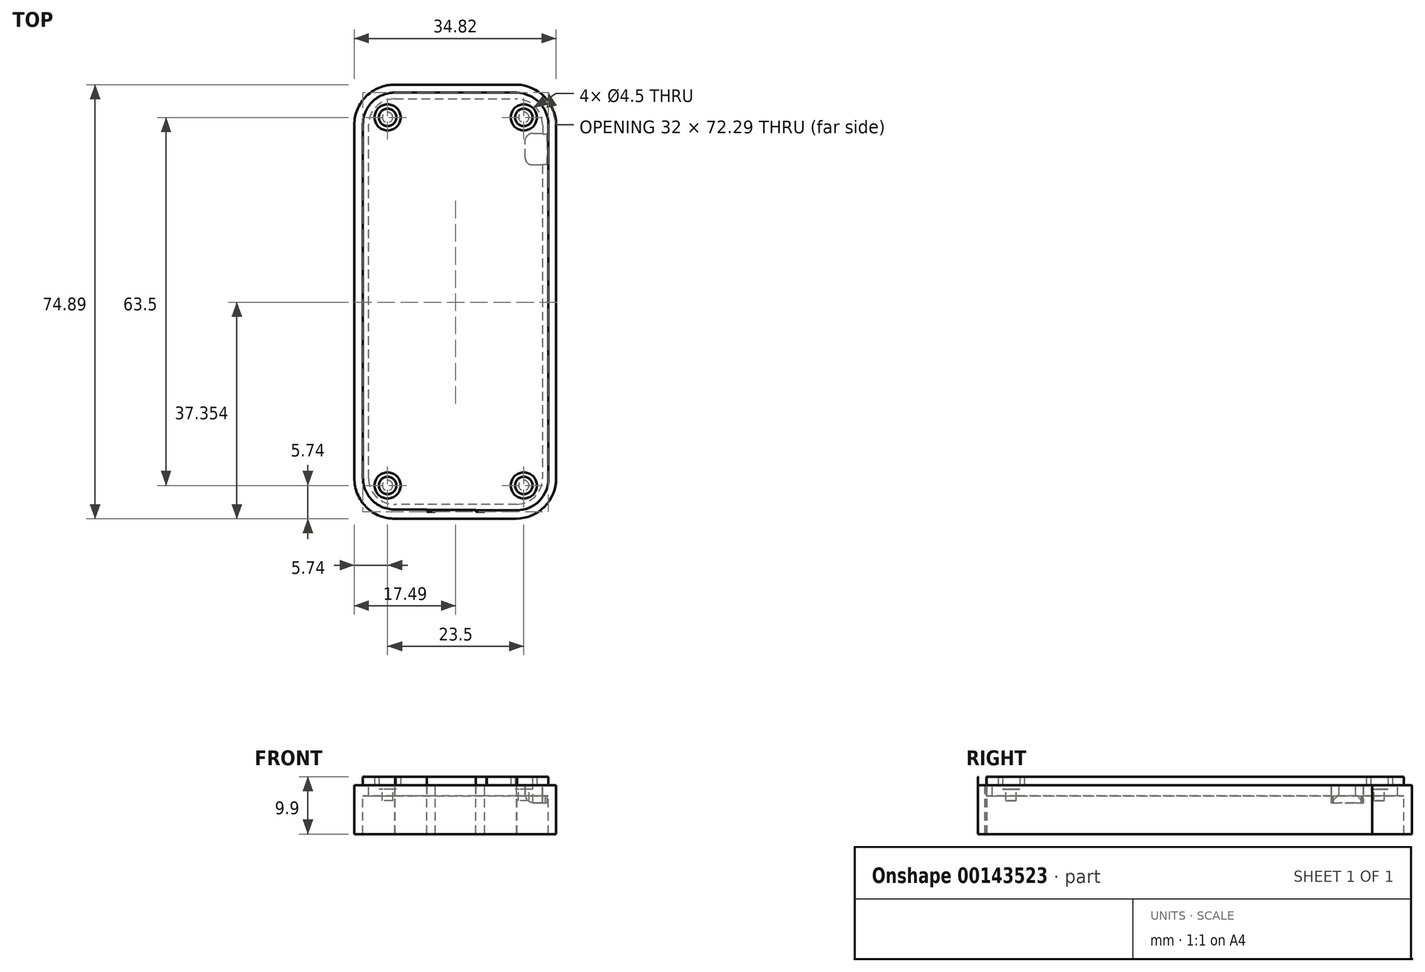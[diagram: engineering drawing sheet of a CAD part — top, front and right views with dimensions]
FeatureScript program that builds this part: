
annotation { "Feature Type Name" : "Feature", "Feature Type Description" : "" }
export const myFeature = defineFeature(function(context is Context, id is Id, definition is map)
    precondition{}
    {
        {
            var Q0;
            Q0=qCreatedBy(makeId("Top.planeOp"),FACE);
            var sketch = newSketch(context, id + "F0", { "sketchPlane" : qUnion([Q0])});
            skFitSpline(sketch, "E0", {"points": [v(15.77, 28.65) * mm, v(15.77, 28.68) * mm, v(15.76, 28.7) * mm, v(15.73, 28.76) * mm, v(15.71, 28.78) * mm, v(15.66, 28.82) * mm, v(15.62, 28.83) * mm, v(15.55, 28.85) * mm, v(15.5, 28.85) * mm, v(15.47, 28.85) * mm]});
            skFitSpline(sketch, "E1", {"points": [v(15.47, 23.65) * mm, v(15.5, 23.65) * mm, v(15.55, 23.65) * mm, v(15.62, 23.67) * mm, v(15.66, 23.68) * mm, v(15.71, 23.72) * mm, v(15.73, 23.74) * mm, v(15.76, 23.8) * mm, v(15.77, 23.82) * mm, v(15.77, 23.85) * mm]});
            skLineSegment(sketch, "E2", {"start": v(-3.5, -35.98) * mm, "end": v(3.5, -35.98) * mm});
            skLineSegment(sketch, "E3", {"start": v(-5.37, -37.49) * mm, "end": v(5.33, -37.49) * mm});
            skLineSegment(sketch, "E4", {"start": v(-5, -37.09) * mm, "end": v(-5, -36.28) * mm});
            skLineSegment(sketch, "E5", {"start": v(5, -36.02) * mm, "end": v(5, -37.12) * mm});
            skArc(sketch, "E6", {"start": v(5, -37.12) * mm, "mid": v(5.1, -37.4) * mm, "end": v(5.4, -37.49) * mm});
            skArc(sketch, "E7", {"start": v(-5.32, -37.49) * mm, "mid": v(-5.08, -37.35) * mm, "end": v(-5, -37.09) * mm});
            skLineSegment(sketch, "E8", {"start": v(14.96, 23.65) * mm, "end": v(15.42, 23.65) * mm});
            skLineSegment(sketch, "E9", {"start": v(15.01, 28.85) * mm, "end": v(15.47, 28.85) * mm});
            skLineSegment(sketch, "E10", {"start": v(14.96, 23.5) * mm, "end": v(14.96, 23.5) * mm});
            skLineSegment(sketch, "E11", {"start": v(14.96, 23.5) * mm, "end": v(13.33, 23.5) * mm});
            skEllipticalArc(sketch, "E12", {});
            skLineSegment(sketch, "E13", {"start": v(15, 29) * mm, "end": v(14.96, 29) * mm});
            skEllipticalArc(sketch, "E14", {});
            skLineSegment(sketch, "E15", {"start": v(13.33, 29) * mm, "end": v(14.96, 29) * mm});
            skFitSpline(sketch, "E16", {"points": [v(12, 27.7) * mm, v(12, 27.86) * mm, v(12.04, 28.05) * mm, v(12.16, 28.35) * mm, v(12.27, 28.5) * mm, v(12.5, 28.73) * mm, v(12.67, 28.84) * mm, v(12.97, 28.96) * mm, v(13.17, 29) * mm, v(13.33, 29) * mm]});
            skFitSpline(sketch, "E17", {"points": [v(13.33, 23.5) * mm, v(13.17, 23.5) * mm, v(12.97, 23.54) * mm, v(12.67, 23.66) * mm, v(12.5, 23.77) * mm, v(12.27, 24) * mm, v(12.16, 24.15) * mm, v(12.04, 24.45) * mm, v(12, 24.64) * mm, v(12, 24.8) * mm]});
            skEllipticalArc(sketch, "E18", {});
            skLineSegment(sketch, "E19", {"start": v(14.96, 23.65) * mm, "end": v(14.96, -30.5) * mm});
            skArc(sketch, "E20", {"start": v(10.53, -35.01) * mm, "mid": v(13.68, -33.67) * mm, "end": v(14.96, -30.5) * mm});
            skLineSegment(sketch, "E21", {"start": v(10.53, -35.01) * mm, "end": v(-10.47, -35.01) * mm});
            skArc(sketch, "E22", {"start": v(-15.01, -30.5) * mm, "mid": v(-13.69, -33.71) * mm, "end": v(-10.47, -35.01) * mm});
            skLineSegment(sketch, "E23", {"start": v(-15.01, -30.5) * mm, "end": v(-15.01, 30.5) * mm});
            skArc(sketch, "E24", {"start": v(-10.5, 34.93) * mm, "mid": v(-13.68, 33.65) * mm, "end": v(-15.01, 30.5) * mm});
            skLineSegment(sketch, "E25", {"start": v(-10.5, 34.93) * mm, "end": v(10.5, 34.93) * mm});
            skArc(sketch, "E26", {"start": v(15.01, 30.38) * mm, "mid": v(13.68, 33.58) * mm, "end": v(10.5, 34.93) * mm});
            skLineSegment(sketch, "E27", {"start": v(15.01, 30.38) * mm, "end": v(15.01, 28.87) * mm});
            skLineSegment(sketch, "E28", {"start": v(-5.37, -35.9) * mm, "end": v(-10.47, -35.9) * mm});
            skArc(sketch, "E29", {"start": v(-16, -30.4) * mm, "mid": v(-14.38, -34.31) * mm, "end": v(-10.47, -35.9) * mm});
            skLineSegment(sketch, "E30", {"start": v(-16, -30.4) * mm, "end": v(-16, 30.6) * mm});
            skArc(sketch, "E31", {"start": v(-10.5, 36) * mm, "mid": v(-14.37, 34.45) * mm, "end": v(-16, 30.6) * mm});
            skLineSegment(sketch, "E32", {"start": v(-10.5, 36) * mm, "end": v(10.5, 36) * mm});
            skArc(sketch, "E33", {"start": v(16, 30.48) * mm, "mid": v(14.38, 34.37) * mm, "end": v(10.5, 36) * mm});
            skLineSegment(sketch, "E34", {"start": v(16, 30.48) * mm, "end": v(16, -30.52) * mm});
            skArc(sketch, "E35", {"start": v(10.59, -36.02) * mm, "mid": v(14.43, -34.39) * mm, "end": v(16, -30.52) * mm});
            skLineSegment(sketch, "E36", {"start": v(5, -36.28) * mm, "end": v(3.5, -36.28) * mm});
            skLineSegment(sketch, "E37", {"start": v(3.5, -36.28) * mm, "end": v(3.5, -35.98) * mm});
            skLineSegment(sketch, "E38", {"start": v(-3.5, -35.98) * mm, "end": v(-3.5, -36.28) * mm});
            skLineSegment(sketch, "E39", {"start": v(-3.5, -36.28) * mm, "end": v(-5, -36.28) * mm});
            skLineSegment(sketch, "E40", {"start": v(15.78, 27.7) * mm, "end": v(15.78, 24.8) * mm});
            skLineSegment(sketch, "E41", {"start": v(12, 24.8) * mm, "end": v(12, 27.7) * mm});
            skCircle(sketch, "E42", {"center": v(-11.75, -31.75) * mm, "radius": 0.9 * mm});
            skCircle(sketch, "E43", {"center": v(11.75, -31.75) * mm, "radius": 0.9 * mm});
            skCircle(sketch, "E44", {"center": v(-11.75, 31.75) * mm, "radius": 0.9 * mm});
            skCircle(sketch, "E45", {"center": v(11.75, 31.75) * mm, "radius": 0.9 * mm});
            skCircle(sketch, "E46", {"center": v(11.75, -31.75) * mm, "radius": 1.5 * mm});
            skCircle(sketch, "E47", {"center": v(-11.75, -31.75) * mm, "radius": 1.5 * mm});
            skCircle(sketch, "E48", {"center": v(11.75, 31.75) * mm, "radius": 1.5 * mm});
            skCircle(sketch, "E49", {"center": v(-11.75, 31.75) * mm, "radius": 1.5 * mm});
            skCircle(sketch, "E50", {"center": v(11.75, -31.75) * mm, "radius": 2.25 * mm});
            skCircle(sketch, "E51", {"center": v(-11.75, -31.75) * mm, "radius": 2.25 * mm});
            skCircle(sketch, "E52", {"center": v(11.75, 31.75) * mm, "radius": 2.25 * mm});
            skCircle(sketch, "E53", {"center": v(-11.75, 31.75) * mm, "radius": 2.25 * mm});
            skLineSegment(sketch, "E54", {"start": v(10.43, -37.49) * mm, "end": v(5.33, -37.49) * mm});
            skLineSegment(sketch, "E55", {"start": v(-5.37, -37.49) * mm, "end": v(-10.47, -37.49) * mm});
            skArc(sketch, "E56", {"start": v(-17.49, -30.5) * mm, "mid": v(-15.44, -35.46) * mm, "end": v(-10.47, -37.49) * mm});
            skLineSegment(sketch, "E57", {"start": v(-17.49, -30.5) * mm, "end": v(-17.49, 30.5) * mm});
            skArc(sketch, "E58", {"start": v(-10.5, 37.4) * mm, "mid": v(-15.43, 35.4) * mm, "end": v(-17.49, 30.5) * mm});
            skLineSegment(sketch, "E59", {"start": v(-10.5, 37.4) * mm, "end": v(10.5, 37.4) * mm});
            skArc(sketch, "E60", {"start": v(17.33, 30.5) * mm, "mid": v(15.3, 35.31) * mm, "end": v(10.5, 37.4) * mm});
            skLineSegment(sketch, "E61", {"start": v(17.33, 30.5) * mm, "end": v(17.33, -30.5) * mm});
            skArc(sketch, "E62", {"start": v(10.43, -37.49) * mm, "mid": v(15.32, -35.42) * mm, "end": v(17.33, -30.5) * mm});
            skLineSegment(sketch, "E63", {"start": v(0, 41.24) * mm, "end": v(0, -41.23) * mm});
            skLineSegment(sketch, "E64", {"start": v(-21.24, 0) * mm, "end": v(21.24, 0) * mm});
            skPoint(sketch, "E65", {"position": v(0, 0) * mm});
            skLineSegment(sketch, "E66", {"start": v(15.42, 23.65) * mm, "end": v(15.47, 23.65) * mm});
            skLineSegment(sketch, "E67", {"start": v(15, 29) * mm, "end": v(15.01, 29) * mm});
            skLineSegment(sketch, "E68", {"start": v(15.01, 28.87) * mm, "end": v(15.01, 28.85) * mm});
            skLineSegment(sketch, "E69", {"start": v(15.01, 28.85) * mm, "end": v(15.01, 28.85) * mm});
            skPoint(sketch, "E70.start.orphan", {"position": v(5.48, -36.02) * mm});
            skLineSegment(sketch, "E71", {"start": v(5, -36.02) * mm, "end": v(10.59, -36.02) * mm});
            skPoint(sketch, "E72.end.orphan", {"position": v(5.48, -36.12) * mm});
            skLineSegment(sketch, "E73", {"start": v(-3.5, -35.98) * mm, "end": v(-5, -35.98) * mm});
            skLineSegment(sketch, "E74", {"start": v(5, -36.02) * mm, "end": v(3.5, -36.02) * mm});
            skPoint(sketch, "E75.orphan", {"position": v(-5, -35.99) * mm});
            skPoint(sketch, "E76.end.orphan", {"position": v(-5, -35.9) * mm});
            skLineSegment(sketch, "E77", {"start": v(-5.37, -35.9) * mm, "end": v(-5, -35.9) * mm});
            skLineSegment(sketch, "E78", {"start": v(-5, -35.9) * mm, "end": v(-5, -35.99) * mm});
            skLineSegment(sketch, "E79", {"start": v(-5, -35.99) * mm, "end": v(-5, -36.28) * mm});
            const initialGuessF0  = {"E12": [0.014993356668767627, 0.024800051225866745, 0, -1, 0.0013, 4.5397e-05, 0.4793271302138709, 0.479729], "E14": [0.015737164668767626, 0.02770005122586673, 0, -1, 0.0013, 4.5397e-05, 1.5707963267948966, 2.388012], "E18": [0.015737164668767626, 0.024800051225866745, 0, -1, 0.0013, 4.5397e-05, 0.75358, 1.5707963267948966]};
            skSetInitialGuess(sketch, initialGuessF0);
            skSolve(sketch);
        }
        {
            var Q0;
            {var subQ1=sQuery(id+"F0.wireOp",EDGE,"E22");Q0=makeQuery(id+"F0.imprint","IMPRINT",FACE,{"disambiguationData":[TD([[makeQuery(id+"F0.imprint","IMPRINT",EDGE,{"derivedFrom":subQ1}),1.0]])]});}
            var Q1;
            {var subQ1=sQuery(id+"F0.wireOp",EDGE,"E20");Q1=makeQuery(id+"F0.imprint","IMPRINT",FACE,{"disambiguationData":[TD([[makeQuery(id+"F0.imprint","IMPRINT",EDGE,{"derivedFrom":subQ1}),1.0]])]});}
            var Q2;
            {var subQ5=sQuery(id+"F0.wireOp",EDGE,"E22");Q2=makeQuery(id+"F0.imprint","IMPRINT",FACE,{"disambiguationData":[TD([[makeQuery(id+"F0.imprint","IMPRINT",EDGE,{"derivedFrom":subQ5}),-1.0]])]});}
            var Q3;
            {var subQ14=sQuery(id+"F0.wireOp",EDGE,"E20");Q3=makeQuery(id+"F0.imprint","IMPRINT",FACE,{"disambiguationData":[TD([[makeQuery(id+"F0.imprint","IMPRINT",EDGE,{"derivedFrom":subQ14}),-1.0]])]});}
            var Q4;
            {var subQ5=sQuery(id+"F0.wireOp",EDGE,"E10");Q4=makeQuery(id+"F0.imprint","IMPRINT",FACE,{"disambiguationData":[TD([[makeQuery(id+"F0.imprint","IMPRINT",EDGE,{"derivedFrom":subQ5}),-1.0]])]});}
            var Q5;
            {var subQ1=sQuery(id+"F0.wireOp",EDGE,"E24");Q5=makeQuery(id+"F0.imprint","IMPRINT",FACE,{"disambiguationData":[TD([[makeQuery(id+"F0.imprint","IMPRINT",EDGE,{"derivedFrom":subQ1}),1.0]])]});}
            var Q6;
            Q6=makeQuery(id+"F0.imprint","IMPRINT",FACE,{"disambiguationData":[TD([[makeQuery(id+"F0.imprint","IMPRINT",EDGE,{"derivedFrom":sQuery(id+"F0.wireOp",EDGE,"E0")}),1.0]])]});
            var Q7;
            Q7=makeQuery(id+"F0.imprint","IMPRINT",FACE,{"disambiguationData":[TD([[makeQuery(id+"F0.imprint","IMPRINT",EDGE,{"derivedFrom":sQuery(id+"F0.wireOp",EDGE,"E0")}),-1.0]])]});
            var Q8;
            {var subQ5=sQuery(id+"F0.wireOp",EDGE,"E24");Q8=makeQuery(id+"F0.imprint","IMPRINT",FACE,{"disambiguationData":[TD([[makeQuery(id+"F0.imprint","IMPRINT",EDGE,{"derivedFrom":subQ5}),-1.0]])]});}
            var Q9;
            Q9=makeQuery(id+"F0.imprint","IMPRINT",FACE,{"disambiguationData":[TD([[makeQuery(id+"F0.imprint","IMPRINT",EDGE,{"derivedFrom":sQuery(id+"F0.wireOp",EDGE,"E48")}),1.0]])]});
            var Q10;
            Q10=makeQuery(id+"F0.imprint","IMPRINT",FACE,{"disambiguationData":[TD([[makeQuery(id+"F0.imprint","IMPRINT",EDGE,{"derivedFrom":sQuery(id+"F0.wireOp",EDGE,"E46")}),1.0]])]});
            var Q11;
            Q11=makeQuery(id+"F0.imprint","IMPRINT",FACE,{"disambiguationData":[TD([[makeQuery(id+"F0.imprint","IMPRINT",EDGE,{"derivedFrom":sQuery(id+"F0.wireOp",EDGE,"E43")}),1.0]])]});
            var Q12;
            Q12=makeQuery(id+"F0.imprint","IMPRINT",FACE,{"disambiguationData":[TD([[makeQuery(id+"F0.imprint","IMPRINT",EDGE,{"derivedFrom":sQuery(id+"F0.wireOp",EDGE,"E47")}),1.0]])]});
            var Q13;
            Q13=makeQuery(id+"F0.imprint","IMPRINT",FACE,{"disambiguationData":[TD([[makeQuery(id+"F0.imprint","IMPRINT",EDGE,{"derivedFrom":sQuery(id+"F0.wireOp",EDGE,"E45")}),1.0]])]});
            var Q14;
            Q14=makeQuery(id+"F0.imprint","IMPRINT",FACE,{"disambiguationData":[TD([[makeQuery(id+"F0.imprint","IMPRINT",EDGE,{"derivedFrom":sQuery(id+"F0.wireOp",EDGE,"E42")}),1.0]])]});
            var Q15;
            Q15=makeQuery(id+"F0.imprint","IMPRINT",FACE,{"disambiguationData":[TD([[makeQuery(id+"F0.imprint","IMPRINT",EDGE,{"derivedFrom":sQuery(id+"F0.wireOp",EDGE,"E49")}),1.0]])]});
            var Q16;
            Q16=makeQuery(id+"F0.imprint","IMPRINT",FACE,{"disambiguationData":[TD([[makeQuery(id+"F0.imprint","IMPRINT",EDGE,{"derivedFrom":sQuery(id+"F0.wireOp",EDGE,"E44")}),1.0]])]});
            var Q17;
            Q17=makeQuery(id+"F0.imprint","IMPRINT",FACE,{"disambiguationData":[TD([[makeQuery(id+"F0.imprint","IMPRINT",EDGE,{"derivedFrom":sQuery(id+"F0.wireOp",EDGE,"E45")}),-1.0]])]});
            var Q18;
            Q18=makeQuery(id+"F0.imprint","IMPRINT",FACE,{"disambiguationData":[TD([[makeQuery(id+"F0.imprint","IMPRINT",EDGE,{"derivedFrom":sQuery(id+"F0.wireOp",EDGE,"E44")}),-1.0]])]});
            var Q19;
            Q19=makeQuery(id+"F0.imprint","IMPRINT",FACE,{"disambiguationData":[TD([[makeQuery(id+"F0.imprint","IMPRINT",EDGE,{"derivedFrom":sQuery(id+"F0.wireOp",EDGE,"E42")}),-1.0]])]});
            var Q20;
            Q20=makeQuery(id+"F0.imprint","IMPRINT",FACE,{"disambiguationData":[TD([[makeQuery(id+"F0.imprint","IMPRINT",EDGE,{"derivedFrom":sQuery(id+"F0.wireOp",EDGE,"E43")}),-1.0]])]});
            var Q21;
            {var subQ0=sQuery(id+"F0.wireOp",EDGE,"E54");var subQ1=sQuery(id+"F0.wireOp",EDGE,"E3");var subQ2=makeQuery(id+"F0.imprint","INTERSECT",VERTEX,{"derivedFrom":[subQ1,subQ0]});Q21=makeQuery(id+"F0.imprint","IMPRINT",FACE,{"disambiguationData":[TD([[makeQuery(id+"F0.imprint","IMPRINT",EDGE,{"disambiguationData":[TD([[subQ2,1.0]])],"derivedFrom":subQ1}),-1.0]])]});}
            extrude(context, id + "F1", {"entities" : qUnion([Q0, Q1, Q2, Q3, Q4, Q5, Q6, Q7, Q8, Q9, Q10, Q11, Q12, Q13, Q14, Q15, Q16, Q17, Q18, Q19, Q20, Q21]), "depth" : 1.5 * mm});
        }
        {
            var Q0;
            {var subQ14=sQuery(id+"F0.wireOp",EDGE,"E20");Q0=makeQuery(id+"F0.imprint","IMPRINT",FACE,{"disambiguationData":[TD([[makeQuery(id+"F0.imprint","IMPRINT",EDGE,{"derivedFrom":subQ14}),-1.0]])]});}
            var Q1;
            Q1=makeQuery(id+"F0.imprint","IMPRINT",FACE,{"disambiguationData":[TD([[makeQuery(id+"F0.imprint","IMPRINT",EDGE,{"derivedFrom":sQuery(id+"F0.wireOp",EDGE,"E0")}),-1.0]])]});
            var Q2;
            {var subQ5=sQuery(id+"F0.wireOp",EDGE,"E24");Q2=makeQuery(id+"F0.imprint","IMPRINT",FACE,{"disambiguationData":[TD([[makeQuery(id+"F0.imprint","IMPRINT",EDGE,{"derivedFrom":subQ5}),-1.0]])]});}
            var Q3;
            {var subQ5=sQuery(id+"F0.wireOp",EDGE,"E22");Q3=makeQuery(id+"F0.imprint","IMPRINT",FACE,{"disambiguationData":[TD([[makeQuery(id+"F0.imprint","IMPRINT",EDGE,{"derivedFrom":subQ5}),-1.0]])]});}
            extrude(context, id + "F2", {"entities" : qUnion([Q0, Q1, Q2, Q3]), "operationType" : NewBodyOperationType.ADD, "oppositeDirection" : true, "depth" : 1.8 * mm});
        }
        {
            var Q0;
            {var subQ4=sQuery(id+"F0.wireOp",EDGE,"E31");Q0=makeQuery(id+"F0.imprint","IMPRINT",FACE,{"disambiguationData":[TD([[makeQuery(id+"F0.imprint","IMPRINT",EDGE,{"derivedFrom":subQ4}),-1.0]])]});}
            var Q1;
            {var subQ1=sQuery(id+"F0.wireOp",EDGE,"E33");Q1=makeQuery(id+"F0.imprint","IMPRINT",FACE,{"disambiguationData":[TD([[makeQuery(id+"F0.imprint","IMPRINT",EDGE,{"derivedFrom":subQ1}),-1.0]])]});}
            var Q2;
            {var subQ7=sQuery(id+"F0.wireOp",EDGE,"E35");Q2=makeQuery(id+"F0.imprint","IMPRINT",FACE,{"disambiguationData":[TD([[makeQuery(id+"F0.imprint","IMPRINT",EDGE,{"derivedFrom":subQ7}),-1.0]])]});}
            var Q3;
            {var subQ5=sQuery(id+"F0.wireOp",EDGE,"E36");Q3=makeQuery(id+"F0.imprint","IMPRINT",FACE,{"disambiguationData":[TD([[makeQuery(id+"F0.imprint","IMPRINT",EDGE,{"derivedFrom":subQ5}),1.0]])]});}
            var Q4;
            {var subQ0=sQuery(id+"F0.wireOp",EDGE,"E7");Q4=makeQuery(id+"F0.imprint","IMPRINT",FACE,{"disambiguationData":[TD([[makeQuery(id+"F0.imprint","IMPRINT",EDGE,{"derivedFrom":subQ0}),-1.0]])]});}
            var Q5;
            {var subQ1=sQuery(id+"F0.wireOp",EDGE,"E7");Q5=makeQuery(id+"F0.imprint","IMPRINT",FACE,{"disambiguationData":[TD([[makeQuery(id+"F0.imprint","IMPRINT",EDGE,{"derivedFrom":subQ1}),1.0]])]});}
            extrude(context, id + "F3", {"entities" : qUnion([Q0, Q1, Q2, Q3, Q4, Q5]), "operationType" : NewBodyOperationType.ADD, "oppositeDirection" : true, "depth" : 8.4 * mm});
        }
        {
            var Q0;
            Q0=makeQuery(id+"F0.imprint","IMPRINT",FACE,{"disambiguationData":[TD([[makeQuery(id+"F0.imprint","IMPRINT",EDGE,{"derivedFrom":sQuery(id+"F0.wireOp",EDGE,"E0")}),1.0]])]});
            extrude(context, id + "F4", {"entities" : qUnion([Q0]), "operationType" : NewBodyOperationType.ADD, "oppositeDirection" : true, "depth" : 3 * mm});
        }
        {
            var Q0;
            Q0=makeQuery(id+"F4.opExtrude","CAP_EDGE",EDGE,{"disambiguationData":[OSD([sQuery(id+"F0.wireOp",EDGE,"E41")])],"isStart":false});
            var Q1;
            Q1=makeQuery(id+"F4.opExtrude","CAP_EDGE",EDGE,{"disambiguationData":[OSD([sQuery(id+"F0.wireOp",EDGE,"E17")])],"isStart":false});
            var Q2;
            Q2=makeQuery(id+"F4.opExtrude","CAP_EDGE",EDGE,{"disambiguationData":[OSD([sQuery(id+"F0.wireOp",EDGE,"E16")])],"isStart":false});
            fillet(context, id + "F5", {"entities" : qUnion([Q0, Q1, Q2]), "radius" : 1.4 * mm, "tangentPropagation" : true, "allowEdgeOverflow" : false});
        }
        {
            var Q0;
            Q0=makeQuery(id+"F0.imprint","IMPRINT",FACE,{"disambiguationData":[TD([[makeQuery(id+"F0.imprint","IMPRINT",EDGE,{"derivedFrom":sQuery(id+"F0.wireOp",EDGE,"E47")}),1.0]])]});
            var Q1;
            Q1=makeQuery(id+"F0.imprint","IMPRINT",FACE,{"disambiguationData":[TD([[makeQuery(id+"F0.imprint","IMPRINT",EDGE,{"derivedFrom":sQuery(id+"F0.wireOp",EDGE,"E46")}),1.0]])]});
            var Q2;
            Q2=makeQuery(id+"F0.imprint","IMPRINT",FACE,{"disambiguationData":[TD([[makeQuery(id+"F0.imprint","IMPRINT",EDGE,{"derivedFrom":sQuery(id+"F0.wireOp",EDGE,"E48")}),1.0]])]});
            var Q3;
            Q3=makeQuery(id+"F0.imprint","IMPRINT",FACE,{"disambiguationData":[TD([[makeQuery(id+"F0.imprint","IMPRINT",EDGE,{"derivedFrom":sQuery(id+"F0.wireOp",EDGE,"E49")}),1.0]])]});
            extrude(context, id + "F6", {"entities" : qUnion([Q0, Q1, Q2, Q3]), "operationType" : NewBodyOperationType.ADD, "oppositeDirection" : true, "depth" : .6618 * mm});
        }
        {
            var Q0;
            Q0=makeQuery(id+"F0.imprint","IMPRINT",FACE,{"disambiguationData":[TD([[makeQuery(id+"F0.imprint","IMPRINT",EDGE,{"derivedFrom":sQuery(id+"F0.wireOp",EDGE,"E42")}),1.0]])]});
            var Q1;
            Q1=makeQuery(id+"F0.imprint","IMPRINT",FACE,{"disambiguationData":[TD([[makeQuery(id+"F0.imprint","IMPRINT",EDGE,{"derivedFrom":sQuery(id+"F0.wireOp",EDGE,"E43")}),1.0]])]});
            var Q2;
            Q2=makeQuery(id+"F0.imprint","IMPRINT",FACE,{"disambiguationData":[TD([[makeQuery(id+"F0.imprint","IMPRINT",EDGE,{"derivedFrom":sQuery(id+"F0.wireOp",EDGE,"E44")}),1.0]])]});
            var Q3;
            Q3=makeQuery(id+"F0.imprint","IMPRINT",FACE,{"disambiguationData":[TD([[makeQuery(id+"F0.imprint","IMPRINT",EDGE,{"derivedFrom":sQuery(id+"F0.wireOp",EDGE,"E45")}),1.0]])]});
            extrude(context, id + "F7", {"entities" : qUnion([Q0, Q1, Q2, Q3]), "operationType" : NewBodyOperationType.ADD, "oppositeDirection" : true, "depth" : 2.66 * mm});
        }
    });
